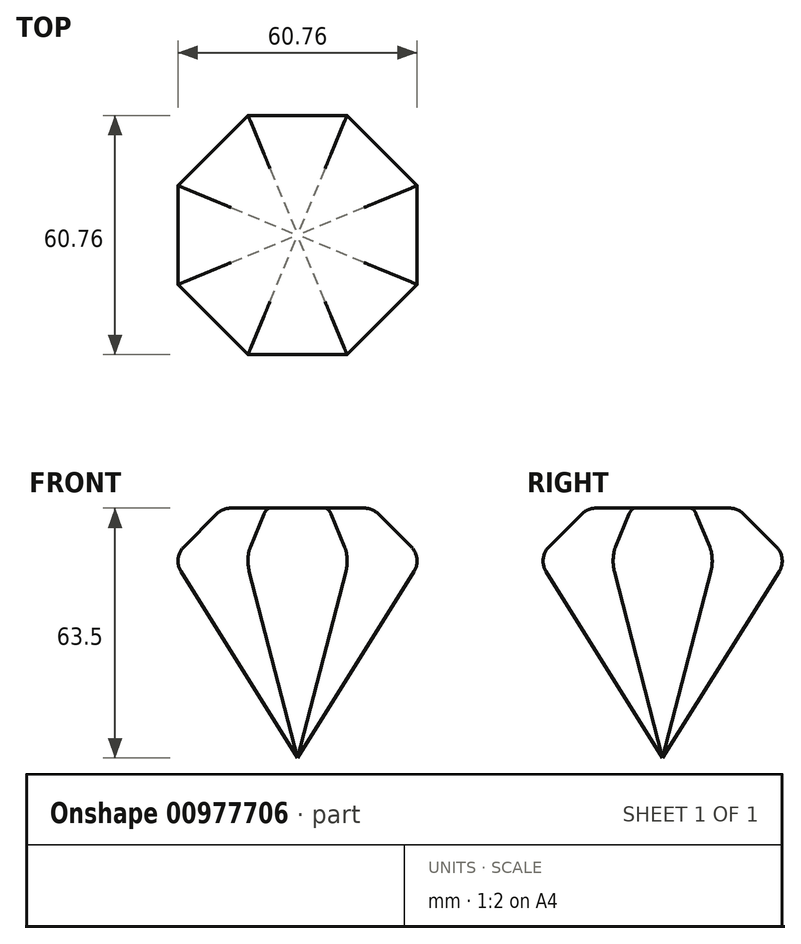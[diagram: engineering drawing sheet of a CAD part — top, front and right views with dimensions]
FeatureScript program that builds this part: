
annotation { "Feature Type Name" : "Feature", "Feature Type Description" : "" }
export const myFeature = defineFeature(function(context is Context, id is Id, definition is map)
    precondition{}
    {
        {
            var Q0;
            Q0=qCreatedBy(makeId("Top.planeOp"),FACE);
            var sketch = newSketch(context, id + "F0", { "sketchPlane" : qUnion([Q0])});
            skCircle(sketch, "E0.cCircle", {"center": v(0, 0) * mm, "radius": 31.75 * mm, "construction": true});
            skLineSegment(sketch, "E0.0", {"start": v(-31.75, -13.15) * mm, "end": v(-31.75, 13.15) * mm});
            skLineSegment(sketch, "E0.1", {"start": v(-31.75, 13.15) * mm, "end": v(-13.15, 31.75) * mm});
            skLineSegment(sketch, "E0.2", {"start": v(-13.15, 31.75) * mm, "end": v(13.15, 31.75) * mm});
            skLineSegment(sketch, "E0.3", {"start": v(13.15, 31.75) * mm, "end": v(31.75, 13.15) * mm});
            skLineSegment(sketch, "E0.4", {"start": v(31.75, 13.15) * mm, "end": v(31.75, -13.15) * mm});
            skLineSegment(sketch, "E0.5", {"start": v(31.75, -13.15) * mm, "end": v(13.15, -31.75) * mm});
            skLineSegment(sketch, "E0.6", {"start": v(13.15, -31.75) * mm, "end": v(-13.15, -31.75) * mm});
            skLineSegment(sketch, "E0.7", {"start": v(-13.15, -31.75) * mm, "end": v(-31.75, -13.15) * mm});
            skPoint(sketch, "E0.0.midPoint", {"position": v(-31.75, 0) * mm});
            skSolve(sketch);
        }
        {
            var Q0;
            Q0=makeQuery(id+"F0.imprint","IMPRINT",FACE,{"disambiguationData":[TD([[makeQuery(id+"F0.imprint","IMPRINT",EDGE,{"derivedFrom":sQuery(id+"F0.wireOp",EDGE,"E0.0")}),-1.0]])]});
            extrude(context, id + "F1", {"entities" : qUnion([Q0]), "depth" : 12.7 * mm, "offsetDistance" : 25.4 * mm});
        }
        {
            var Q0;
            Q0=makeQuery(id+"F1.opExtrude","CAP_FACE",FACE,{"disambiguationData":[OSD([sQuery(id+"F0.wireOp",EDGE,"E0.0"),sQuery(id+"F0.wireOp",EDGE,"E0.1"),sQuery(id+"F0.wireOp",EDGE,"E0.2"),sQuery(id+"F0.wireOp",EDGE,"E0.3"),sQuery(id+"F0.wireOp",EDGE,"E0.4"),sQuery(id+"F0.wireOp",EDGE,"E0.5"),sQuery(id+"F0.wireOp",EDGE,"E0.6"),sQuery(id+"F0.wireOp",EDGE,"E0.7")])],"isStart":false});
            chamfer(context, id + "F2", {"entities" : qUnion([Q0]), "chamferType" : ChamferType.OFFSET_ANGLE, "width" : 12.7 * mm, "oppositeDirection" : false, "angle" : 45 * degree, "tangentPropagation" : true});
        }
        {
            var Q0;
            Q0=makeQuery(id+"F1.opExtrude","CAP_FACE",FACE,{"disambiguationData":[OSD([sQuery(id+"F0.wireOp",EDGE,"E0.0"),sQuery(id+"F0.wireOp",EDGE,"E0.1"),sQuery(id+"F0.wireOp",EDGE,"E0.2"),sQuery(id+"F0.wireOp",EDGE,"E0.3"),sQuery(id+"F0.wireOp",EDGE,"E0.4"),sQuery(id+"F0.wireOp",EDGE,"E0.5"),sQuery(id+"F0.wireOp",EDGE,"E0.6"),sQuery(id+"F0.wireOp",EDGE,"E0.7")])],"isStart":true});
            cPlane(context, id + "F3", {"entities" : qUnion([Q0]), "cplaneType" : CPlaneType.OFFSET, "offset" : 50.8 * mm, "width" : 152.4 * mm, "height" : 152.4 * mm});
        }
        {
            var Q0;
            Q0=qCreatedBy(id+"F3.planeOp",FACE);
            var sketch = newSketch(context, id + "F4", { "sketchPlane" : qUnion([Q0])});
            skPoint(sketch, "E1", {"position": v(0, 0) * mm});
            skSolve(sketch);
        }
        {
            var Q1;
            Q1=makeQuery(id+"F1.opExtrude","CAP_FACE",FACE,{"disambiguationData":[OSD([sQuery(id+"F0.wireOp",EDGE,"E0.0"),sQuery(id+"F0.wireOp",EDGE,"E0.1"),sQuery(id+"F0.wireOp",EDGE,"E0.2"),sQuery(id+"F0.wireOp",EDGE,"E0.3"),sQuery(id+"F0.wireOp",EDGE,"E0.4"),sQuery(id+"F0.wireOp",EDGE,"E0.5"),sQuery(id+"F0.wireOp",EDGE,"E0.6"),sQuery(id+"F0.wireOp",EDGE,"E0.7")])],"isStart":true});
            var Q2;
            Q2=sQuery(id+"F4.wireOp",VERTEX,"E1");
            loft(context, id + "F5", {"operationType" : NewBodyOperationType.ADD, "sheetProfilesArray" : [{ "sheetProfileEntities" : qUnion([Q1]) }, { "sheetProfileEntities" : qUnion([Q2]) }]});
        }
        {
            var Q0;
            Q0=makeQuery(id+"F1.opExtrude","CAP_FACE",FACE,{"disambiguationData":[OSD([sQuery(id+"F0.wireOp",EDGE,"E0.0"),sQuery(id+"F0.wireOp",EDGE,"E0.1"),sQuery(id+"F0.wireOp",EDGE,"E0.2"),sQuery(id+"F0.wireOp",EDGE,"E0.3"),sQuery(id+"F0.wireOp",EDGE,"E0.4"),sQuery(id+"F0.wireOp",EDGE,"E0.5"),sQuery(id+"F0.wireOp",EDGE,"E0.6"),sQuery(id+"F0.wireOp",EDGE,"E0.7")])],"isStart":false});
            var Q1;
            {var subQ0=sQuery(id+"F0.wireOp",EDGE,"E0.7");var subQ1=sQuery(id+"F0.wireOp",EDGE,"E0.6");var subQ2=sQuery(id+"F0.wireOp",EDGE,"E0.5");var subQ3=sQuery(id+"F0.wireOp",EDGE,"E0.4");var subQ4=sQuery(id+"F0.wireOp",EDGE,"E0.3");var subQ5=sQuery(id+"F0.wireOp",EDGE,"E0.2");var subQ6=sQuery(id+"F0.wireOp",EDGE,"E0.1");var subQ7=sQuery(id+"F0.wireOp",EDGE,"E0.0");var subQ8=makeQuery(id+"F1.opExtrude","CAP_FACE",FACE,{"disambiguationData":[OSD([subQ7,subQ6,subQ5,subQ4,subQ3,subQ2,subQ1,subQ0])],"isStart":true});var subQ9=makeQuery(id+"F1.opExtrude","CAP_EDGE",EDGE,{"disambiguationData":[OSD([subQ1])],"isStart":false});var subQ10=makeQuery(id+"F2.opChamfer","BLEND_EDGE",EDGE,{"blendedFrom":[subQ9,subQ8],"blendedInto":[subQ8]});Q1=makeQuery(id+"F5.boolean.opBoolean","MERGE",EDGE,{"derivedFrom":[subQ10,makeQuery(id+"F5.opLoft","MID_CAP_EDGE",EDGE,{"disambiguationData":[OSD([subQ7,subQ6,subQ5,subQ4,subQ3,subQ2,subQ1,subQ0]),TDD([makeQuery(id+"F2.opChamfer","BLEND_VERTEX",VERTEX,{"blendedFrom":[makeQuery(id+"F1.opExtrude","CAP_EDGE",EDGE,{"disambiguationData":[OSD([subQ2])],"isStart":false}),subQ9,subQ8],"blendedInto":[subQ8]}),makeQuery(id+"F2.opChamfer","BLEND_VERTEX",VERTEX,{"blendedFrom":[subQ9,makeQuery(id+"F1.opExtrude","CAP_EDGE",EDGE,{"disambiguationData":[OSD([subQ0])],"isStart":false}),subQ8],"blendedInto":[subQ8]}),subQ10])],"capPos":0.0})]});}
            var Q2;
            {var subQ0=sQuery(id+"F0.wireOp",EDGE,"E0.7");var subQ1=sQuery(id+"F0.wireOp",EDGE,"E0.6");var subQ2=sQuery(id+"F0.wireOp",EDGE,"E0.5");var subQ3=sQuery(id+"F0.wireOp",EDGE,"E0.4");var subQ4=sQuery(id+"F0.wireOp",EDGE,"E0.3");var subQ5=sQuery(id+"F0.wireOp",EDGE,"E0.2");var subQ6=sQuery(id+"F0.wireOp",EDGE,"E0.1");var subQ7=sQuery(id+"F0.wireOp",EDGE,"E0.0");var subQ8=makeQuery(id+"F1.opExtrude","CAP_FACE",FACE,{"disambiguationData":[OSD([subQ7,subQ6,subQ5,subQ4,subQ3,subQ2,subQ1,subQ0])],"isStart":true});var subQ9=makeQuery(id+"F1.opExtrude","CAP_EDGE",EDGE,{"disambiguationData":[OSD([subQ2])],"isStart":false});var subQ10=makeQuery(id+"F2.opChamfer","BLEND_EDGE",EDGE,{"blendedFrom":[subQ9,subQ8],"blendedInto":[subQ8]});Q2=makeQuery(id+"F5.boolean.opBoolean","MERGE",EDGE,{"derivedFrom":[subQ10,makeQuery(id+"F5.opLoft","MID_CAP_EDGE",EDGE,{"disambiguationData":[OSD([subQ7,subQ6,subQ5,subQ4,subQ3,subQ2,subQ1,subQ0]),TDD([makeQuery(id+"F2.opChamfer","BLEND_VERTEX",VERTEX,{"blendedFrom":[makeQuery(id+"F1.opExtrude","CAP_EDGE",EDGE,{"disambiguationData":[OSD([subQ3])],"isStart":false}),subQ9,subQ8],"blendedInto":[subQ8]}),makeQuery(id+"F2.opChamfer","BLEND_VERTEX",VERTEX,{"blendedFrom":[subQ9,makeQuery(id+"F1.opExtrude","CAP_EDGE",EDGE,{"disambiguationData":[OSD([subQ1])],"isStart":false}),subQ8],"blendedInto":[subQ8]}),subQ10])],"capPos":0.0})]});}
            var Q3;
            {var subQ0=sQuery(id+"F0.wireOp",EDGE,"E0.7");var subQ1=sQuery(id+"F0.wireOp",EDGE,"E0.6");var subQ2=sQuery(id+"F0.wireOp",EDGE,"E0.5");var subQ3=sQuery(id+"F0.wireOp",EDGE,"E0.4");var subQ4=sQuery(id+"F0.wireOp",EDGE,"E0.3");var subQ5=sQuery(id+"F0.wireOp",EDGE,"E0.2");var subQ6=sQuery(id+"F0.wireOp",EDGE,"E0.1");var subQ7=sQuery(id+"F0.wireOp",EDGE,"E0.0");var subQ8=makeQuery(id+"F1.opExtrude","CAP_FACE",FACE,{"disambiguationData":[OSD([subQ7,subQ6,subQ5,subQ4,subQ3,subQ2,subQ1,subQ0])],"isStart":true});var subQ9=makeQuery(id+"F1.opExtrude","CAP_EDGE",EDGE,{"disambiguationData":[OSD([subQ3])],"isStart":false});var subQ10=makeQuery(id+"F2.opChamfer","BLEND_EDGE",EDGE,{"blendedFrom":[subQ9,subQ8],"blendedInto":[subQ8]});Q3=makeQuery(id+"F5.boolean.opBoolean","MERGE",EDGE,{"derivedFrom":[subQ10,makeQuery(id+"F5.opLoft","MID_CAP_EDGE",EDGE,{"disambiguationData":[OSD([subQ7,subQ6,subQ5,subQ4,subQ3,subQ2,subQ1,subQ0]),TDD([makeQuery(id+"F2.opChamfer","BLEND_VERTEX",VERTEX,{"blendedFrom":[makeQuery(id+"F1.opExtrude","CAP_EDGE",EDGE,{"disambiguationData":[OSD([subQ4])],"isStart":false}),subQ9,subQ8],"blendedInto":[subQ8]}),makeQuery(id+"F2.opChamfer","BLEND_VERTEX",VERTEX,{"blendedFrom":[subQ9,makeQuery(id+"F1.opExtrude","CAP_EDGE",EDGE,{"disambiguationData":[OSD([subQ2])],"isStart":false}),subQ8],"blendedInto":[subQ8]}),subQ10])],"capPos":0.0})]});}
            var Q4;
            {var subQ0=sQuery(id+"F0.wireOp",EDGE,"E0.7");var subQ1=sQuery(id+"F0.wireOp",EDGE,"E0.6");var subQ2=sQuery(id+"F0.wireOp",EDGE,"E0.5");var subQ3=sQuery(id+"F0.wireOp",EDGE,"E0.4");var subQ4=sQuery(id+"F0.wireOp",EDGE,"E0.3");var subQ5=sQuery(id+"F0.wireOp",EDGE,"E0.2");var subQ6=sQuery(id+"F0.wireOp",EDGE,"E0.1");var subQ7=sQuery(id+"F0.wireOp",EDGE,"E0.0");var subQ8=makeQuery(id+"F1.opExtrude","CAP_FACE",FACE,{"disambiguationData":[OSD([subQ7,subQ6,subQ5,subQ4,subQ3,subQ2,subQ1,subQ0])],"isStart":true});var subQ9=makeQuery(id+"F1.opExtrude","CAP_EDGE",EDGE,{"disambiguationData":[OSD([subQ4])],"isStart":false});var subQ10=makeQuery(id+"F2.opChamfer","BLEND_EDGE",EDGE,{"blendedFrom":[subQ9,subQ8],"blendedInto":[subQ8]});Q4=makeQuery(id+"F5.boolean.opBoolean","MERGE",EDGE,{"derivedFrom":[subQ10,makeQuery(id+"F5.opLoft","MID_CAP_EDGE",EDGE,{"disambiguationData":[OSD([subQ7,subQ6,subQ5,subQ4,subQ3,subQ2,subQ1,subQ0]),TDD([makeQuery(id+"F2.opChamfer","BLEND_VERTEX",VERTEX,{"blendedFrom":[makeQuery(id+"F1.opExtrude","CAP_EDGE",EDGE,{"disambiguationData":[OSD([subQ5])],"isStart":false}),subQ9,subQ8],"blendedInto":[subQ8]}),makeQuery(id+"F2.opChamfer","BLEND_VERTEX",VERTEX,{"blendedFrom":[subQ9,makeQuery(id+"F1.opExtrude","CAP_EDGE",EDGE,{"disambiguationData":[OSD([subQ3])],"isStart":false}),subQ8],"blendedInto":[subQ8]}),subQ10])],"capPos":0.0})]});}
            var Q5;
            {var subQ0=sQuery(id+"F0.wireOp",EDGE,"E0.7");var subQ1=sQuery(id+"F0.wireOp",EDGE,"E0.6");var subQ2=sQuery(id+"F0.wireOp",EDGE,"E0.5");var subQ3=sQuery(id+"F0.wireOp",EDGE,"E0.4");var subQ4=sQuery(id+"F0.wireOp",EDGE,"E0.3");var subQ5=sQuery(id+"F0.wireOp",EDGE,"E0.2");var subQ6=sQuery(id+"F0.wireOp",EDGE,"E0.1");var subQ7=sQuery(id+"F0.wireOp",EDGE,"E0.0");var subQ8=makeQuery(id+"F1.opExtrude","CAP_FACE",FACE,{"disambiguationData":[OSD([subQ7,subQ6,subQ5,subQ4,subQ3,subQ2,subQ1,subQ0])],"isStart":true});var subQ9=makeQuery(id+"F1.opExtrude","CAP_EDGE",EDGE,{"disambiguationData":[OSD([subQ0])],"isStart":false});var subQ10=makeQuery(id+"F2.opChamfer","BLEND_EDGE",EDGE,{"blendedFrom":[subQ9,subQ8],"blendedInto":[subQ8]});Q5=makeQuery(id+"F5.boolean.opBoolean","MERGE",EDGE,{"derivedFrom":[subQ10,makeQuery(id+"F5.opLoft","MID_CAP_EDGE",EDGE,{"disambiguationData":[OSD([subQ7,subQ6,subQ5,subQ4,subQ3,subQ2,subQ1,subQ0]),TDD([makeQuery(id+"F2.opChamfer","BLEND_VERTEX",VERTEX,{"blendedFrom":[makeQuery(id+"F1.opExtrude","CAP_EDGE",EDGE,{"disambiguationData":[OSD([subQ7])],"isStart":false}),subQ9,subQ8],"blendedInto":[subQ8]}),makeQuery(id+"F2.opChamfer","BLEND_VERTEX",VERTEX,{"blendedFrom":[makeQuery(id+"F1.opExtrude","CAP_EDGE",EDGE,{"disambiguationData":[OSD([subQ1])],"isStart":false}),subQ9,subQ8],"blendedInto":[subQ8]}),subQ10])],"capPos":0.0})]});}
            var Q6;
            {var subQ0=sQuery(id+"F0.wireOp",EDGE,"E0.7");var subQ1=sQuery(id+"F0.wireOp",EDGE,"E0.6");var subQ2=sQuery(id+"F0.wireOp",EDGE,"E0.5");var subQ3=sQuery(id+"F0.wireOp",EDGE,"E0.4");var subQ4=sQuery(id+"F0.wireOp",EDGE,"E0.3");var subQ5=sQuery(id+"F0.wireOp",EDGE,"E0.2");var subQ6=sQuery(id+"F0.wireOp",EDGE,"E0.1");var subQ7=sQuery(id+"F0.wireOp",EDGE,"E0.0");var subQ8=makeQuery(id+"F1.opExtrude","CAP_FACE",FACE,{"disambiguationData":[OSD([subQ7,subQ6,subQ5,subQ4,subQ3,subQ2,subQ1,subQ0])],"isStart":true});var subQ9=makeQuery(id+"F1.opExtrude","CAP_EDGE",EDGE,{"disambiguationData":[OSD([subQ7])],"isStart":false});var subQ10=makeQuery(id+"F2.opChamfer","BLEND_EDGE",EDGE,{"blendedFrom":[subQ9,subQ8],"blendedInto":[subQ8]});Q6=makeQuery(id+"F5.boolean.opBoolean","MERGE",EDGE,{"derivedFrom":[subQ10,makeQuery(id+"F5.opLoft","MID_CAP_EDGE",EDGE,{"disambiguationData":[OSD([subQ7,subQ6,subQ5,subQ4,subQ3,subQ2,subQ1,subQ0]),TDD([makeQuery(id+"F2.opChamfer","BLEND_VERTEX",VERTEX,{"blendedFrom":[subQ9,makeQuery(id+"F1.opExtrude","CAP_EDGE",EDGE,{"disambiguationData":[OSD([subQ6])],"isStart":false}),subQ8],"blendedInto":[subQ8]}),makeQuery(id+"F2.opChamfer","BLEND_VERTEX",VERTEX,{"blendedFrom":[subQ9,makeQuery(id+"F1.opExtrude","CAP_EDGE",EDGE,{"disambiguationData":[OSD([subQ0])],"isStart":false}),subQ8],"blendedInto":[subQ8]}),subQ10])],"capPos":0.0})]});}
            var Q7;
            {var subQ0=sQuery(id+"F0.wireOp",EDGE,"E0.7");var subQ1=sQuery(id+"F0.wireOp",EDGE,"E0.6");var subQ2=sQuery(id+"F0.wireOp",EDGE,"E0.5");var subQ3=sQuery(id+"F0.wireOp",EDGE,"E0.4");var subQ4=sQuery(id+"F0.wireOp",EDGE,"E0.3");var subQ5=sQuery(id+"F0.wireOp",EDGE,"E0.2");var subQ6=sQuery(id+"F0.wireOp",EDGE,"E0.1");var subQ7=sQuery(id+"F0.wireOp",EDGE,"E0.0");var subQ8=makeQuery(id+"F1.opExtrude","CAP_FACE",FACE,{"disambiguationData":[OSD([subQ7,subQ6,subQ5,subQ4,subQ3,subQ2,subQ1,subQ0])],"isStart":true});var subQ9=makeQuery(id+"F1.opExtrude","CAP_EDGE",EDGE,{"disambiguationData":[OSD([subQ6])],"isStart":false});var subQ10=makeQuery(id+"F2.opChamfer","BLEND_EDGE",EDGE,{"blendedFrom":[subQ9,subQ8],"blendedInto":[subQ8]});Q7=makeQuery(id+"F5.boolean.opBoolean","MERGE",EDGE,{"derivedFrom":[subQ10,makeQuery(id+"F5.opLoft","MID_CAP_EDGE",EDGE,{"disambiguationData":[OSD([subQ7,subQ6,subQ5,subQ4,subQ3,subQ2,subQ1,subQ0]),TDD([makeQuery(id+"F2.opChamfer","BLEND_VERTEX",VERTEX,{"blendedFrom":[makeQuery(id+"F1.opExtrude","CAP_EDGE",EDGE,{"disambiguationData":[OSD([subQ7])],"isStart":false}),subQ9,subQ8],"blendedInto":[subQ8]}),makeQuery(id+"F2.opChamfer","BLEND_VERTEX",VERTEX,{"blendedFrom":[subQ9,makeQuery(id+"F1.opExtrude","CAP_EDGE",EDGE,{"disambiguationData":[OSD([subQ5])],"isStart":false}),subQ8],"blendedInto":[subQ8]}),subQ10])],"capPos":0.0})]});}
            var Q8;
            {var subQ0=sQuery(id+"F0.wireOp",EDGE,"E0.7");var subQ1=sQuery(id+"F0.wireOp",EDGE,"E0.6");var subQ2=sQuery(id+"F0.wireOp",EDGE,"E0.5");var subQ3=sQuery(id+"F0.wireOp",EDGE,"E0.4");var subQ4=sQuery(id+"F0.wireOp",EDGE,"E0.3");var subQ5=sQuery(id+"F0.wireOp",EDGE,"E0.2");var subQ6=sQuery(id+"F0.wireOp",EDGE,"E0.1");var subQ7=sQuery(id+"F0.wireOp",EDGE,"E0.0");var subQ8=makeQuery(id+"F1.opExtrude","CAP_FACE",FACE,{"disambiguationData":[OSD([subQ7,subQ6,subQ5,subQ4,subQ3,subQ2,subQ1,subQ0])],"isStart":true});var subQ9=makeQuery(id+"F1.opExtrude","CAP_EDGE",EDGE,{"disambiguationData":[OSD([subQ5])],"isStart":false});var subQ10=makeQuery(id+"F2.opChamfer","BLEND_EDGE",EDGE,{"blendedFrom":[subQ9,subQ8],"blendedInto":[subQ8]});Q8=makeQuery(id+"F5.boolean.opBoolean","MERGE",EDGE,{"derivedFrom":[subQ10,makeQuery(id+"F5.opLoft","MID_CAP_EDGE",EDGE,{"disambiguationData":[OSD([subQ7,subQ6,subQ5,subQ4,subQ3,subQ2,subQ1,subQ0]),TDD([makeQuery(id+"F2.opChamfer","BLEND_VERTEX",VERTEX,{"blendedFrom":[makeQuery(id+"F1.opExtrude","CAP_EDGE",EDGE,{"disambiguationData":[OSD([subQ6])],"isStart":false}),subQ9,subQ8],"blendedInto":[subQ8]}),makeQuery(id+"F2.opChamfer","BLEND_VERTEX",VERTEX,{"blendedFrom":[subQ9,makeQuery(id+"F1.opExtrude","CAP_EDGE",EDGE,{"disambiguationData":[OSD([subQ4])],"isStart":false}),subQ8],"blendedInto":[subQ8]}),subQ10])],"capPos":0.0})]});}
            fillet(context, id + "F6", {"entities" : qUnion([Q0, Q1, Q2, Q3, Q4, Q5, Q6, Q7, Q8]), "radius" : 5.08 * mm, "tangentPropagation" : true, "allowEdgeOverflow" : false});
        }
    });
